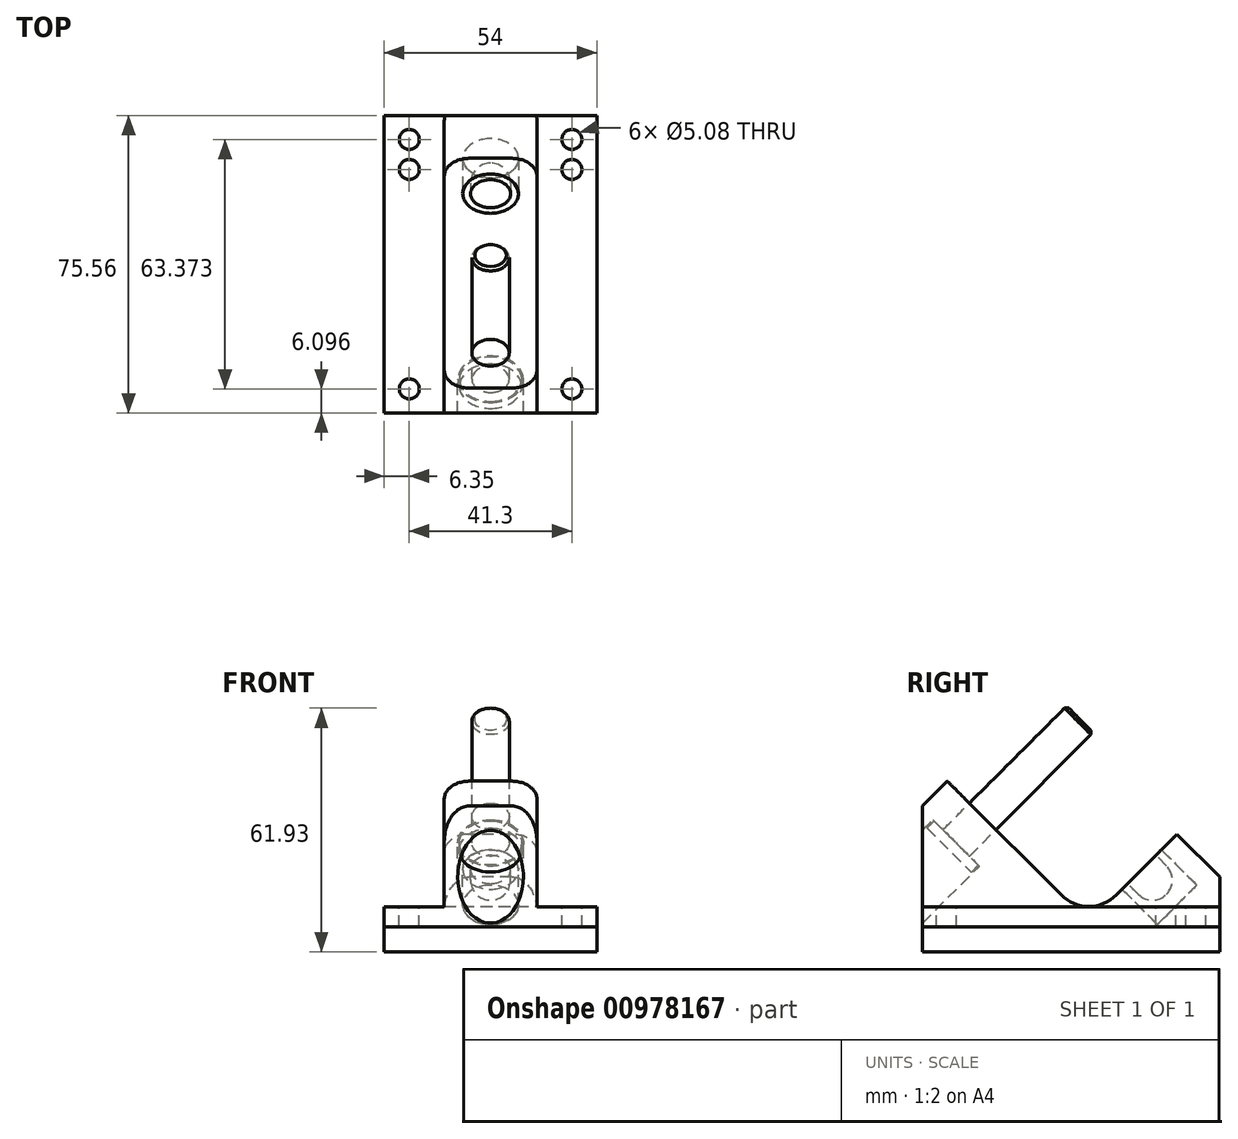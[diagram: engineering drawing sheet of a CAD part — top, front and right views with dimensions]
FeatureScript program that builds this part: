
annotation { "Feature Type Name" : "Feature", "Feature Type Description" : "" }
export const myFeature = defineFeature(function(context is Context, id is Id, definition is map)
    precondition{}
    {
        {
            var Q0;
            Q0=qCreatedBy(makeId("Right.planeOp"),FACE);
            var sketch = newSketch(context, id + "F0", { "sketchPlane" : qUnion([Q0])});
            skLineSegment(sketch, "E0", {"start": v(0, 0) * mm, "end": v(0, 30.72) * mm});
            skLineSegment(sketch, "E1", {"start": v(0, 30.72) * mm, "end": v(6.32, 37.04) * mm});
            skLineSegment(sketch, "E2", {"start": v(6.32, 37.04) * mm, "end": v(42.25, 1.12) * mm});
            skLineSegment(sketch, "E3", {"start": v(42.25, 1.12) * mm, "end": v(64.7, 23.57) * mm});
            skLineSegment(sketch, "E4", {"start": v(64.7, 23.57) * mm, "end": v(75.57, 12.7) * mm});
            skLineSegment(sketch, "E5", {"start": v(75.57, 12.7) * mm, "end": v(75.57, 0) * mm});
            skLineSegment(sketch, "E6", {"start": v(75.57, 0) * mm, "end": v(0, 0) * mm});
            skLineSegment(sketch, "E7", {"start": v(15.3, 28.06) * mm, "end": v(28.77, 41.53) * mm, "construction": true});
            skLineSegment(sketch, "E8", {"start": v(28.77, 41.53) * mm, "end": v(64.68, 5.62) * mm, "construction": true});
            skLineSegment(sketch, "E9", {"start": v(64.68, 5.62) * mm, "end": v(69.7, 10.6) * mm, "construction": true});
            skLineSegment(sketch, "E10", {"start": v(69.7, 10.6) * mm, "end": v(60.72, 19.59) * mm, "construction": true});
            skLineSegment(sketch, "E11", {"start": v(28.77, 41.53) * mm, "end": v(15.3, 55) * mm, "construction": true});
            skCircle(sketch, "E12", {"center": v(15.3, 55) * mm, "radius": 4 * mm, "construction": true});
            skLineSegment(sketch, "E13", {"start": v(64.68, 5.62) * mm, "end": v(58.89, -0.13) * mm, "construction": true});
            skLineSegment(sketch, "E14", {"start": v(58.89, -0.13) * mm, "end": v(49.94, 8.81) * mm, "construction": true});
            skCircle(sketch, "E15", {"center": v(58.4, 11.9) * mm, "radius": 5.08 * mm, "construction": true});
            skSolve(sketch);
        }
        {
            var Q0;
            Q0 = qSketchRegion(id + "F0", true);
            extrude(context, id + "F1", {"entities" : qUnion([Q0]), "depth" : 27 * mm, "offsetDistance" : 25.4 * mm});
        }
        {
            var Q0;
            Q0=makeQuery(id+"F1.opExtrude","SWEPT_EDGE",EDGE,{"disambiguationData":[OSD([sQuery(id+"F0.wireOp",EDGE,"E2"),sQuery(id+"F0.wireOp",EDGE,"E3")])]});
            fillet(context, id + "F2", {"entities" : qUnion([Q0]), "radius" : 9.9 * mm, "tangentPropagation" : true, "allowEdgeOverflow" : false});
        }
        {
            var Q0;
            Q0=makeQuery(id+"F1.opExtrude","CAP_FACE",FACE,{"disambiguationData":[OSD([sQuery(id+"F0.wireOp",EDGE,"E0"),sQuery(id+"F0.wireOp",EDGE,"E1"),sQuery(id+"F0.wireOp",EDGE,"E2"),sQuery(id+"F0.wireOp",EDGE,"E3"),sQuery(id+"F0.wireOp",EDGE,"E4"),sQuery(id+"F0.wireOp",EDGE,"E5"),sQuery(id+"F0.wireOp",EDGE,"E6")])],"isStart":false});
            var sketch = newSketch(context, id + "F3", { "sketchPlane" : qUnion([Q0])});
            skLineSegment(sketch, "E16.bottom", {"start": v(0, 5.08) * mm, "end": v(75.57, 5.08) * mm});
            skLineSegment(sketch, "E16.top", {"start": v(0, 37.04) * mm, "end": v(75.57, 37.04) * mm});
            skLineSegment(sketch, "E16.left", {"start": v(0, 5.08) * mm, "end": v(0, 37.04) * mm});
            skLineSegment(sketch, "E16.right", {"start": v(75.57, 5.08) * mm, "end": v(75.57, 37.04) * mm});
            skSolve(sketch);
        }
        {
            var Q0;
            Q0 = qSketchRegion(id + "F3", true);
            extrude(context, id + "F4", {"entities" : qUnion([Q0]), "operationType" : NewBodyOperationType.REMOVE, "oppositeDirection" : true, "depth" : 15.24 * mm, "offsetDistance" : 25.4 * mm});
        }
        {
            var Q0;
            Q0=makeQuery(id+"F4.boolean.opBoolean","COPY",FACE,{"derivedFrom":makeQuery(id+"F4.opExtrude","SWEPT_FACE",FACE,{"disambiguationData":[OSD([sQuery(id+"F3.wireOp",EDGE,"E16.bottom")])]})});
            var sketch = newSketch(context, id + "F5", { "sketchPlane" : qUnion([Q0])});
            skLineSegment(sketch, "E17", {"start": v(20.65, 69.47) * mm, "end": v(20.65, 61.85) * mm, "construction": true});
            skLineSegment(sketch, "E18", {"start": v(20.65, 61.85) * mm, "end": v(20.65, 6.1) * mm, "construction": true});
            skCircle(sketch, "E19", {"center": v(20.65, 69.47) * mm, "radius": 2.54 * mm});
            skCircle(sketch, "E20", {"center": v(20.65, 61.85) * mm, "radius": 2.54 * mm});
            skCircle(sketch, "E21", {"center": v(20.65, 6.1) * mm, "radius": 2.54 * mm});
            skSolve(sketch);
        }
        {
            var Q0;
            Q0=makeQuery(id+"F5.imprint","IMPRINT",FACE,{"disambiguationData":[TD([[makeQuery(id+"F5.imprint","IMPRINT",EDGE,{"derivedFrom":sQuery(id+"F5.wireOp",EDGE,"E19")}),1.0]])]});
            var Q1;
            Q1=makeQuery(id+"F5.imprint","IMPRINT",FACE,{"disambiguationData":[TD([[makeQuery(id+"F5.imprint","IMPRINT",EDGE,{"derivedFrom":sQuery(id+"F5.wireOp",EDGE,"E20")}),1.0]])]});
            var Q2;
            Q2=makeQuery(id+"F5.imprint","IMPRINT",FACE,{"disambiguationData":[TD([[makeQuery(id+"F5.imprint","IMPRINT",EDGE,{"derivedFrom":sQuery(id+"F5.wireOp",EDGE,"E21")}),1.0]])]});
            extrude(context, id + "F6", {"entities" : qUnion([Q0, Q1, Q2]), "operationType" : NewBodyOperationType.REMOVE, "endBound" : BoundingType.THROUGH_ALL, "oppositeDirection" : true, "depth" : 25.4 * mm, "offsetDistance" : 25.4 * mm});
        }
        {
            var Q0;
            Q0=makeQuery(id+"F1.opExtrude","SWEPT_BODY",BODY,{"disambiguationData":[OSD([sQuery(id+"F0.wireOp",EDGE,"E0"),sQuery(id+"F0.wireOp",EDGE,"E1"),sQuery(id+"F0.wireOp",EDGE,"E2"),sQuery(id+"F0.wireOp",EDGE,"E3"),sQuery(id+"F0.wireOp",EDGE,"E4"),sQuery(id+"F0.wireOp",EDGE,"E5"),sQuery(id+"F0.wireOp",EDGE,"E6")])]});
            var Q1;
            Q1=makeQuery(id+"F1.opExtrude","CAP_FACE",FACE,{"disambiguationData":[OSD([sQuery(id+"F0.wireOp",EDGE,"E0"),sQuery(id+"F0.wireOp",EDGE,"E1"),sQuery(id+"F0.wireOp",EDGE,"E2"),sQuery(id+"F0.wireOp",EDGE,"E3"),sQuery(id+"F0.wireOp",EDGE,"E4"),sQuery(id+"F0.wireOp",EDGE,"E5"),sQuery(id+"F0.wireOp",EDGE,"E6")])],"isStart":true});
            mirror(context, id + "F7", {"operationType" : NewBodyOperationType.ADD, "entities" : qUnion([Q0]), "mirrorPlane" : qUnion([Q1])});
        }
        {
            var Q0;
            Q0=makeQuery(id+"F4.boolean.opBoolean","INTERSECT",EDGE,{"derivedFrom":[makeQuery(id+"F1.opExtrude","SWEPT_FACE",FACE,{"disambiguationData":[OSD([sQuery(id+"F0.wireOp",EDGE,"E1")])]}),makeQuery(id+"F4.opExtrude","CAP_FACE",FACE,{"disambiguationData":[OSD([sQuery(id+"F3.wireOp",EDGE,"E16.bottom"),sQuery(id+"F3.wireOp",EDGE,"E16.top"),sQuery(id+"F3.wireOp",EDGE,"E16.left"),sQuery(id+"F3.wireOp",EDGE,"E16.right")])],"isStart":false})]});
            var Q1;
            Q1=makeQuery(id+"F7.opPattern","COPY",EDGE,{"derivedFrom":makeQuery(id+"F4.boolean.opBoolean","INTERSECT",EDGE,{"derivedFrom":[makeQuery(id+"F1.opExtrude","SWEPT_FACE",FACE,{"disambiguationData":[OSD([sQuery(id+"F0.wireOp",EDGE,"E1")])]}),makeQuery(id+"F4.opExtrude","CAP_FACE",FACE,{"disambiguationData":[OSD([sQuery(id+"F3.wireOp",EDGE,"E16.bottom"),sQuery(id+"F3.wireOp",EDGE,"E16.top"),sQuery(id+"F3.wireOp",EDGE,"E16.left"),sQuery(id+"F3.wireOp",EDGE,"E16.right")])],"isStart":false})]}),"instanceName":"1"});
            var Q2;
            Q2=makeQuery(id+"F4.boolean.opBoolean","INTERSECT",EDGE,{"derivedFrom":[makeQuery(id+"F1.opExtrude","SWEPT_FACE",FACE,{"disambiguationData":[OSD([sQuery(id+"F0.wireOp",EDGE,"E4")])]}),makeQuery(id+"F4.opExtrude","CAP_FACE",FACE,{"disambiguationData":[OSD([sQuery(id+"F3.wireOp",EDGE,"E16.bottom"),sQuery(id+"F3.wireOp",EDGE,"E16.top"),sQuery(id+"F3.wireOp",EDGE,"E16.left"),sQuery(id+"F3.wireOp",EDGE,"E16.right")])],"isStart":false})]});
            var Q3;
            Q3=makeQuery(id+"F7.opPattern","COPY",EDGE,{"derivedFrom":makeQuery(id+"F4.boolean.opBoolean","INTERSECT",EDGE,{"derivedFrom":[makeQuery(id+"F1.opExtrude","SWEPT_FACE",FACE,{"disambiguationData":[OSD([sQuery(id+"F0.wireOp",EDGE,"E4")])]}),makeQuery(id+"F4.opExtrude","CAP_FACE",FACE,{"disambiguationData":[OSD([sQuery(id+"F3.wireOp",EDGE,"E16.bottom"),sQuery(id+"F3.wireOp",EDGE,"E16.top"),sQuery(id+"F3.wireOp",EDGE,"E16.left"),sQuery(id+"F3.wireOp",EDGE,"E16.right")])],"isStart":false})]}),"instanceName":"1"});
            fillet(context, id + "F8", {"entities" : qUnion([Q0, Q1, Q2, Q3]), "radius" : 6.35 * mm, "tangentPropagation" : true, "allowEdgeOverflow" : false});
        }
        {
            var Q0;
            Q0=qCreatedBy(makeId("Right.planeOp"),FACE);
            var sketch = newSketch(context, id + "F9", { "sketchPlane" : qUnion([Q0])});
            skLineSegment(sketch, "E22.0", {"start": v(15.3, 28.06) * mm, "end": v(28.77, 41.53) * mm, "construction": true});
            skLineSegment(sketch, "E23", {"start": v(11.94, 31.43) * mm, "end": v(5.2, 24.7) * mm});
            skLineSegment(sketch, "E24", {"start": v(5.2, 24.7) * mm, "end": v(2.67, 27.22) * mm});
            skLineSegment(sketch, "E25", {"start": v(2.67, 27.22) * mm, "end": v(-18.65, 5.9) * mm});
            skLineSegment(sketch, "E26", {"start": v(-18.65, 5.9) * mm, "end": v(-12.75, 0) * mm});
            skLineSegment(sketch, "E27", {"start": v(-12.75, 0) * mm, "end": v(15.3, 28.06) * mm});
            skLineSegment(sketch, "E28", {"start": v(28.77, 41.53) * mm, "end": v(-12.75, 0) * mm, "construction": true});
            skLineSegment(sketch, "E29", {"start": v(11.94, 31.43) * mm, "end": v(15.3, 28.06) * mm});
            skLineSegment(sketch, "E30", {"start": v(28.77, 41.53) * mm, "end": v(-23.61, -10.86) * mm, "construction": true});
            skSolve(sketch);
        }
        {
            var Q0;
            Q0 = qSketchRegion(id + "F9", true);
            var Q1;
            Q1=sQuery(id+"F9.wireOp",EDGE,"E22.0");
            revolve(context, id + "F10", {"operationType" : NewBodyOperationType.REMOVE, "surfaceOperationType" : NewSurfaceOperationType.NEW, "entities" : qUnion([Q0]), "axis" : qUnion([Q1]), "revolveType" : RevolveType.FULL, "oppositeDirection" : true});
        }
        {
            var Q0;
            Q0=qCreatedBy(makeId("Right.planeOp"),FACE);
            var sketch = newSketch(context, id + "F11", { "sketchPlane" : qUnion([Q0])});
            skLineSegment(sketch, "E31.1", {"start": v(5.2, 24.7) * mm, "end": v(2.96, 26.94) * mm});
            skLineSegment(sketch, "E31.2", {"start": v(11.94, 31.43) * mm, "end": v(5.2, 24.7) * mm});
            skLineSegment(sketch, "E32", {"start": v(2.96, 26.94) * mm, "end": v(1.16, 25.14) * mm});
            skPoint(sketch, "E31.0.end.orphan", {"position": v(-18.65, 5.9) * mm});
            skPoint(sketch, "E31.0.start.orphan", {"position": v(2.67, 27.22) * mm});
            skLineSegment(sketch, "E33", {"start": v(1.16, 25.14) * mm, "end": v(6.77, 19.53) * mm});
            skLineSegment(sketch, "E34", {"start": v(6.77, 19.53) * mm, "end": v(40, 52.75) * mm});
            skLineSegment(sketch, "E35", {"start": v(40, 52.75) * mm, "end": v(36.63, 56.12) * mm});
            skLineSegment(sketch, "E36", {"start": v(36.63, 56.12) * mm, "end": v(11.94, 31.43) * mm});
            skSolve(sketch);
        }
        {
            var Q0;
            Q0 = qSketchRegion(id + "F11", true);
            var Q1;
            Q1=sQuery(id+"F9.wireOp",EDGE,"E30");
            revolve(context, id + "F12", {"surfaceOperationType" : NewSurfaceOperationType.NEW, "entities" : qUnion([Q0]), "axis" : qUnion([Q1]), "revolveType" : RevolveType.FULL});
        }
        {
            var Q0;
            Q0=makeQuery(id+"F12.opRevolve","SWEPT_FACE",FACE,{"disambiguationData":[OSD([sQuery(id+"F11.wireOp",EDGE,"E35")])]});
            chamfer(context, id + "F13", {"entities" : qUnion([Q0]), "width" : 0.76 * mm, "tangentPropagation" : true});
        }
        {
            var Q0;
            Q0=qCreatedBy(makeId("Right.planeOp"),FACE);
            var sketch = newSketch(context, id + "F14", { "sketchPlane" : qUnion([Q0])});
            skLineSegment(sketch, "E37.0", {"start": v(69.7, 10.6) * mm, "end": v(60.72, 19.59) * mm, "construction": true});
            skLineSegment(sketch, "E37.1", {"start": v(64.68, 5.62) * mm, "end": v(69.7, 10.6) * mm, "construction": true});
            skLineSegment(sketch, "E37.2", {"start": v(64.68, 5.62) * mm, "end": v(58.89, -0.13) * mm, "construction": true});
            skLineSegment(sketch, "E37.3", {"start": v(58.89, -0.13) * mm, "end": v(49.94, 8.81) * mm, "construction": true});
            skLineSegment(sketch, "E37.4", {"start": v(28.77, 41.53) * mm, "end": v(64.68, 5.62) * mm, "construction": true});
            skCircle(sketch, "E37.5", {"center": v(58.4, 11.9) * mm, "radius": 5.08 * mm, "construction": true});
            skPoint(sketch, "E37.6", {"position": v(61.78, 2.75) * mm});
            skLineSegment(sketch, "E38", {"start": v(60.72, 19.59) * mm, "end": v(69.7, 10.6) * mm});
            skLineSegment(sketch, "E39", {"start": v(60.72, 19.59) * mm, "end": v(55.72, 14.59) * mm});
            skLineSegment(sketch, "E40", {"start": v(55.72, 14.59) * mm, "end": v(64.68, 5.62) * mm});
            skLineSegment(sketch, "E41", {"start": v(69.7, 10.6) * mm, "end": v(64.68, 5.62) * mm});
            skSolve(sketch);
        }
        {
            var Q0;
            Q0 = qSketchRegion(id + "F14", true);
            var Q1;
            Q1=sQuery(id+"F14.wireOp",EDGE,"E37.4");
            revolve(context, id + "F15", {"operationType" : NewBodyOperationType.REMOVE, "surfaceOperationType" : NewSurfaceOperationType.NEW, "entities" : qUnion([Q0]), "axis" : qUnion([Q1]), "revolveType" : RevolveType.FULL, "oppositeDirection" : true});
        }
        {
            var Q0;
            Q0=qCreatedBy(makeId("Right.planeOp"),FACE);
            var sketch = newSketch(context, id + "F16", { "sketchPlane" : qUnion([Q0])});
            skArc(sketch, "E42.0", {"start": v(62, 8.3) * mm, "mid": v(63.49, 11.9) * mm, "end": v(62, 15.49) * mm});
            skLineSegment(sketch, "E43.0", {"start": v(60.72, 19.59) * mm, "end": v(69.7, 10.6) * mm, "construction": true});
            skLineSegment(sketch, "E43.1", {"start": v(69.7, 10.6) * mm, "end": v(64.68, 5.62) * mm, "construction": true});
            skLineSegment(sketch, "E43.2", {"start": v(55.72, 14.59) * mm, "end": v(64.68, 5.62) * mm, "construction": true});
            skLineSegment(sketch, "E43.3", {"start": v(60.72, 19.59) * mm, "end": v(55.72, 14.59) * mm, "construction": true});
            skLineSegment(sketch, "E44", {"start": v(59.3, 18.18) * mm, "end": v(62, 15.49) * mm, "construction": true});
            skLineSegment(sketch, "E45", {"start": v(62, 15.49) * mm, "end": v(59.3, 18.18) * mm});
            skLineSegment(sketch, "E46", {"start": v(60.72, 19.59) * mm, "end": v(69.7, 10.6) * mm});
            skLineSegment(sketch, "E47", {"start": v(64.68, 5.62) * mm, "end": v(62, 8.3) * mm});
            skLineSegment(sketch, "E48", {"start": v(60.72, 19.59) * mm, "end": v(59.3, 18.18) * mm});
            skLineSegment(sketch, "E49", {"start": v(69.7, 10.6) * mm, "end": v(64.68, 5.62) * mm});
            skSolve(sketch);
        }
        {
            var Q0;
            Q0 = qSketchRegion(id + "F16", true);
            var Q1;
            Q1=sQuery(id+"F14.wireOp",EDGE,"E37.4");
            revolve(context, id + "F17", {"surfaceOperationType" : NewSurfaceOperationType.NEW, "entities" : qUnion([Q0]), "axis" : qUnion([Q1]), "revolveType" : RevolveType.FULL});
        }
        {
            var Q0;
            {var subQ0=makeQuery(id+"F1.opExtrude","SWEPT_FACE",FACE,{"disambiguationData":[OSD([sQuery(id+"F0.wireOp",EDGE,"E6")])]});Q0=makeQuery(id+"F7.boolean.opBoolean","MERGE",FACE,{"derivedFrom":[subQ0,makeQuery(id+"F7.opPattern","COPY",FACE,{"derivedFrom":subQ0,"instanceName":"1"})]});}
            var sketch = newSketch(context, id + "F18", { "sketchPlane" : qUnion([Q0])});
            skLineSegment(sketch, "E50.bottom", {"start": v(-27, 0) * mm, "end": v(27, 0) * mm});
            skLineSegment(sketch, "E50.top", {"start": v(-27, -75.57) * mm, "end": v(27, -75.57) * mm});
            skLineSegment(sketch, "E50.left", {"start": v(-27, 0) * mm, "end": v(-27, -75.57) * mm});
            skLineSegment(sketch, "E50.right", {"start": v(27, 0) * mm, "end": v(27, -75.57) * mm});
            skSolve(sketch);
        }
        {
            var Q0;
            Q0 = qSketchRegion(id + "F18", true);
            extrude(context, id + "F19", {"entities" : qUnion([Q0]), "depth" : 6.35 * mm, "offsetDistance" : 25.4 * mm});
        }
    });
